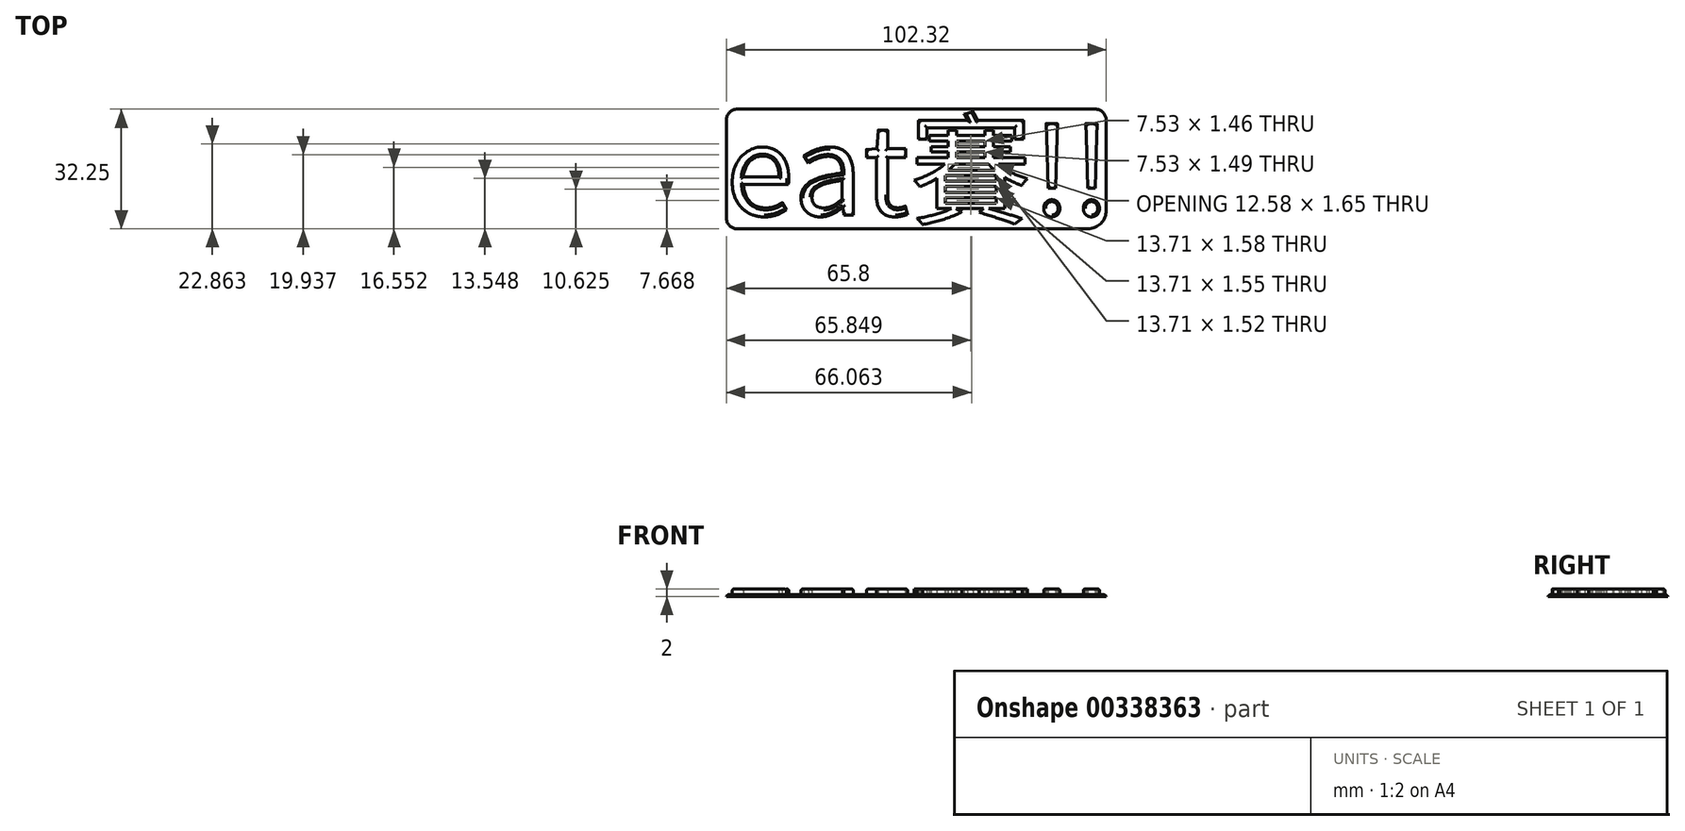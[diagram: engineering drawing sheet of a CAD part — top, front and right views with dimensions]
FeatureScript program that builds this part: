
annotation { "Feature Type Name" : "Feature", "Feature Type Description" : "" }
export const myFeature = defineFeature(function(context is Context, id is Id, definition is map)
    precondition{}
    {
        {
            var Q0;
            Q0=qCreatedBy(makeId("Top.planeOp"),FACE);
            var sketch = newSketch(context, id + "F0", { "sketchPlane" : qUnion([Q0])});
            skText(sketch, "E0", { "text": "eat賽!!", "fontName": "NotoSansCJKtc-Regular.otf"});
            const initialGuessF0  = {"E0": [-0.0526, 0.0191, 1, 0, 0.02378]};
            skSetInitialGuess(sketch, initialGuessF0);
            skSolve(sketch);
        }
        {
            var Q0;
            Q0 = qSketchRegion(id + "F0", true);
            extrude(context, id + "F1", {"entities" : qUnion([Q0]), "depth" : 1.5 * mm});
        }
        {
            var Q0;
            Q0=makeQuery(id+"F1.opExtrude","CAP_FACE",FACE,{"disambiguationData":[OSD([sQuery(id+"F0.wireOp",EDGE,"E0.sketch_text.stroke-0"),sQuery(id+"F0.wireOp",EDGE,"E0.sketch_text.stroke-1"),sQuery(id+"F0.wireOp",EDGE,"E0.sketch_text.stroke-2"),sQuery(id+"F0.wireOp",EDGE,"E0.sketch_text.stroke-3"),sQuery(id+"F0.wireOp",EDGE,"E0.sketch_text.stroke-4"),sQuery(id+"F0.wireOp",EDGE,"E0.sketch_text.stroke-5"),sQuery(id+"F0.wireOp",EDGE,"E0.sketch_text.stroke-6"),sQuery(id+"F0.wireOp",EDGE,"E0.sketch_text.stroke-7"),sQuery(id+"F0.wireOp",EDGE,"E0.sketch_text.stroke-8"),sQuery(id+"F0.wireOp",EDGE,"E0.sketch_text.stroke-9"),sQuery(id+"F0.wireOp",EDGE,"E0.sketch_text.stroke-10"),sQuery(id+"F0.wireOp",EDGE,"E0.sketch_text.stroke-11")])],"isStart":false});
            var Q1;
            Q1=makeQuery(id+"F1.opExtrude","CAP_FACE",FACE,{"disambiguationData":[OSD([sQuery(id+"F0.wireOp",EDGE,"E0.sketch_text.stroke-12"),sQuery(id+"F0.wireOp",EDGE,"E0.sketch_text.stroke-13"),sQuery(id+"F0.wireOp",EDGE,"E0.sketch_text.stroke-14"),sQuery(id+"F0.wireOp",EDGE,"E0.sketch_text.stroke-15"),sQuery(id+"F0.wireOp",EDGE,"E0.sketch_text.stroke-16"),sQuery(id+"F0.wireOp",EDGE,"E0.sketch_text.stroke-17"),sQuery(id+"F0.wireOp",EDGE,"E0.sketch_text.stroke-18"),sQuery(id+"F0.wireOp",EDGE,"E0.sketch_text.stroke-19"),sQuery(id+"F0.wireOp",EDGE,"E0.sketch_text.stroke-20"),sQuery(id+"F0.wireOp",EDGE,"E0.sketch_text.stroke-21"),sQuery(id+"F0.wireOp",EDGE,"E0.sketch_text.stroke-22"),sQuery(id+"F0.wireOp",EDGE,"E0.sketch_text.stroke-23"),sQuery(id+"F0.wireOp",EDGE,"E0.sketch_text.stroke-24"),sQuery(id+"F0.wireOp",EDGE,"E0.sketch_text.stroke-25"),sQuery(id+"F0.wireOp",EDGE,"E0.sketch_text.stroke-26"),sQuery(id+"F0.wireOp",EDGE,"E0.sketch_text.stroke-27")])],"isStart":false});
            var Q2;
            Q2=makeQuery(id+"F1.opExtrude","CAP_FACE",FACE,{"disambiguationData":[OSD([sQuery(id+"F0.wireOp",EDGE,"E0.sketch_text.stroke-28"),sQuery(id+"F0.wireOp",EDGE,"E0.sketch_text.stroke-29"),sQuery(id+"F0.wireOp",EDGE,"E0.sketch_text.stroke-30"),sQuery(id+"F0.wireOp",EDGE,"E0.sketch_text.stroke-31"),sQuery(id+"F0.wireOp",EDGE,"E0.sketch_text.stroke-32"),sQuery(id+"F0.wireOp",EDGE,"E0.sketch_text.stroke-33"),sQuery(id+"F0.wireOp",EDGE,"E0.sketch_text.stroke-34"),sQuery(id+"F0.wireOp",EDGE,"E0.sketch_text.stroke-35"),sQuery(id+"F0.wireOp",EDGE,"E0.sketch_text.stroke-36"),sQuery(id+"F0.wireOp",EDGE,"E0.sketch_text.stroke-37"),sQuery(id+"F0.wireOp",EDGE,"E0.sketch_text.stroke-38"),sQuery(id+"F0.wireOp",EDGE,"E0.sketch_text.stroke-39"),sQuery(id+"F0.wireOp",EDGE,"E0.sketch_text.stroke-40"),sQuery(id+"F0.wireOp",EDGE,"E0.sketch_text.stroke-41"),sQuery(id+"F0.wireOp",EDGE,"E0.sketch_text.stroke-42"),sQuery(id+"F0.wireOp",EDGE,"E0.sketch_text.stroke-43")])],"isStart":false});
            var Q3;
            Q3=makeQuery(id+"F1.opExtrude","CAP_FACE",FACE,{"disambiguationData":[OSD([sQuery(id+"F0.wireOp",EDGE,"E0.sketch_text.stroke-56"),sQuery(id+"F0.wireOp",EDGE,"E0.sketch_text.stroke-57"),sQuery(id+"F0.wireOp",EDGE,"E0.sketch_text.stroke-58"),sQuery(id+"F0.wireOp",EDGE,"E0.sketch_text.stroke-59"),sQuery(id+"F0.wireOp",EDGE,"E0.sketch_text.stroke-60"),sQuery(id+"F0.wireOp",EDGE,"E0.sketch_text.stroke-61"),sQuery(id+"F0.wireOp",EDGE,"E0.sketch_text.stroke-62"),sQuery(id+"F0.wireOp",EDGE,"E0.sketch_text.stroke-63"),sQuery(id+"F0.wireOp",EDGE,"E0.sketch_text.stroke-64"),sQuery(id+"F0.wireOp",EDGE,"E0.sketch_text.stroke-65"),sQuery(id+"F0.wireOp",EDGE,"E0.sketch_text.stroke-66"),sQuery(id+"F0.wireOp",EDGE,"E0.sketch_text.stroke-67"),sQuery(id+"F0.wireOp",EDGE,"E0.sketch_text.stroke-68"),sQuery(id+"F0.wireOp",EDGE,"E0.sketch_text.stroke-69"),sQuery(id+"F0.wireOp",EDGE,"E0.sketch_text.stroke-70"),sQuery(id+"F0.wireOp",EDGE,"E0.sketch_text.stroke-71"),sQuery(id+"F0.wireOp",EDGE,"E0.sketch_text.stroke-72"),sQuery(id+"F0.wireOp",EDGE,"E0.sketch_text.stroke-73"),sQuery(id+"F0.wireOp",EDGE,"E0.sketch_text.stroke-74"),sQuery(id+"F0.wireOp",EDGE,"E0.sketch_text.stroke-75"),sQuery(id+"F0.wireOp",EDGE,"E0.sketch_text.stroke-76"),sQuery(id+"F0.wireOp",EDGE,"E0.sketch_text.stroke-77"),sQuery(id+"F0.wireOp",EDGE,"E0.sketch_text.stroke-78"),sQuery(id+"F0.wireOp",EDGE,"E0.sketch_text.stroke-79"),sQuery(id+"F0.wireOp",EDGE,"E0.sketch_text.stroke-80"),sQuery(id+"F0.wireOp",EDGE,"E0.sketch_text.stroke-81"),sQuery(id+"F0.wireOp",EDGE,"E0.sketch_text.stroke-82"),sQuery(id+"F0.wireOp",EDGE,"E0.sketch_text.stroke-83"),sQuery(id+"F0.wireOp",EDGE,"E0.sketch_text.stroke-84"),sQuery(id+"F0.wireOp",EDGE,"E0.sketch_text.stroke-85"),sQuery(id+"F0.wireOp",EDGE,"E0.sketch_text.stroke-86"),sQuery(id+"F0.wireOp",EDGE,"E0.sketch_text.stroke-87"),sQuery(id+"F0.wireOp",EDGE,"E0.sketch_text.stroke-88"),sQuery(id+"F0.wireOp",EDGE,"E0.sketch_text.stroke-89"),sQuery(id+"F0.wireOp",EDGE,"E0.sketch_text.stroke-90"),sQuery(id+"F0.wireOp",EDGE,"E0.sketch_text.stroke-91"),sQuery(id+"F0.wireOp",EDGE,"E0.sketch_text.stroke-92"),sQuery(id+"F0.wireOp",EDGE,"E0.sketch_text.stroke-93"),sQuery(id+"F0.wireOp",EDGE,"E0.sketch_text.stroke-94"),sQuery(id+"F0.wireOp",EDGE,"E0.sketch_text.stroke-95"),sQuery(id+"F0.wireOp",EDGE,"E0.sketch_text.stroke-96"),sQuery(id+"F0.wireOp",EDGE,"E0.sketch_text.stroke-97"),sQuery(id+"F0.wireOp",EDGE,"E0.sketch_text.stroke-98"),sQuery(id+"F0.wireOp",EDGE,"E0.sketch_text.stroke-99"),sQuery(id+"F0.wireOp",EDGE,"E0.sketch_text.stroke-100"),sQuery(id+"F0.wireOp",EDGE,"E0.sketch_text.stroke-101"),sQuery(id+"F0.wireOp",EDGE,"E0.sketch_text.stroke-102"),sQuery(id+"F0.wireOp",EDGE,"E0.sketch_text.stroke-103"),sQuery(id+"F0.wireOp",EDGE,"E0.sketch_text.stroke-104"),sQuery(id+"F0.wireOp",EDGE,"E0.sketch_text.stroke-105"),sQuery(id+"F0.wireOp",EDGE,"E0.sketch_text.stroke-106"),sQuery(id+"F0.wireOp",EDGE,"E0.sketch_text.stroke-107"),sQuery(id+"F0.wireOp",EDGE,"E0.sketch_text.stroke-108"),sQuery(id+"F0.wireOp",EDGE,"E0.sketch_text.stroke-109"),sQuery(id+"F0.wireOp",EDGE,"E0.sketch_text.stroke-110"),sQuery(id+"F0.wireOp",EDGE,"E0.sketch_text.stroke-111"),sQuery(id+"F0.wireOp",EDGE,"E0.sketch_text.stroke-112"),sQuery(id+"F0.wireOp",EDGE,"E0.sketch_text.stroke-113"),sQuery(id+"F0.wireOp",EDGE,"E0.sketch_text.stroke-114"),sQuery(id+"F0.wireOp",EDGE,"E0.sketch_text.stroke-115"),sQuery(id+"F0.wireOp",EDGE,"E0.sketch_text.stroke-116"),sQuery(id+"F0.wireOp",EDGE,"E0.sketch_text.stroke-117"),sQuery(id+"F0.wireOp",EDGE,"E0.sketch_text.stroke-118"),sQuery(id+"F0.wireOp",EDGE,"E0.sketch_text.stroke-119"),sQuery(id+"F0.wireOp",EDGE,"E0.sketch_text.stroke-120"),sQuery(id+"F0.wireOp",EDGE,"E0.sketch_text.stroke-121"),sQuery(id+"F0.wireOp",EDGE,"E0.sketch_text.stroke-122"),sQuery(id+"F0.wireOp",EDGE,"E0.sketch_text.stroke-123"),sQuery(id+"F0.wireOp",EDGE,"E0.sketch_text.stroke-124"),sQuery(id+"F0.wireOp",EDGE,"E0.sketch_text.stroke-125"),sQuery(id+"F0.wireOp",EDGE,"E0.sketch_text.stroke-126"),sQuery(id+"F0.wireOp",EDGE,"E0.sketch_text.stroke-127")])],"isStart":false});
            var Q4;
            Q4=makeQuery(id+"F1.opExtrude","CAP_FACE",FACE,{"disambiguationData":[OSD([sQuery(id+"F0.wireOp",EDGE,"E0.sketch_text.stroke-44"),sQuery(id+"F0.wireOp",EDGE,"E0.sketch_text.stroke-45"),sQuery(id+"F0.wireOp",EDGE,"E0.sketch_text.stroke-46"),sQuery(id+"F0.wireOp",EDGE,"E0.sketch_text.stroke-47"),sQuery(id+"F0.wireOp",EDGE,"E0.sketch_text.stroke-48"),sQuery(id+"F0.wireOp",EDGE,"E0.sketch_text.stroke-49"),sQuery(id+"F0.wireOp",EDGE,"E0.sketch_text.stroke-50"),sQuery(id+"F0.wireOp",EDGE,"E0.sketch_text.stroke-51"),sQuery(id+"F0.wireOp",EDGE,"E0.sketch_text.stroke-52"),sQuery(id+"F0.wireOp",EDGE,"E0.sketch_text.stroke-53"),sQuery(id+"F0.wireOp",EDGE,"E0.sketch_text.stroke-54"),sQuery(id+"F0.wireOp",EDGE,"E0.sketch_text.stroke-55")])],"isStart":false});
            var Q5;
            Q5=makeQuery(id+"F1.opExtrude","CAP_FACE",FACE,{"disambiguationData":[OSD([sQuery(id+"F0.wireOp",EDGE,"E0.sketch_text.stroke-128"),sQuery(id+"F0.wireOp",EDGE,"E0.sketch_text.stroke-129"),sQuery(id+"F0.wireOp",EDGE,"E0.sketch_text.stroke-130"),sQuery(id+"F0.wireOp",EDGE,"E0.sketch_text.stroke-131"),sQuery(id+"F0.wireOp",EDGE,"E0.sketch_text.stroke-132"),sQuery(id+"F0.wireOp",EDGE,"E0.sketch_text.stroke-133")])],"isStart":false});
            var Q6;
            Q6=makeQuery(id+"F1.opExtrude","CAP_FACE",FACE,{"disambiguationData":[OSD([sQuery(id+"F0.wireOp",EDGE,"E0.sketch_text.stroke-134"),sQuery(id+"F0.wireOp",EDGE,"E0.sketch_text.stroke-135"),sQuery(id+"F0.wireOp",EDGE,"E0.sketch_text.stroke-136"),sQuery(id+"F0.wireOp",EDGE,"E0.sketch_text.stroke-137")])],"isStart":false});
            var Q7;
            Q7=makeQuery(id+"F1.opExtrude","CAP_FACE",FACE,{"disambiguationData":[OSD([sQuery(id+"F0.wireOp",EDGE,"E0.sketch_text.stroke-144"),sQuery(id+"F0.wireOp",EDGE,"E0.sketch_text.stroke-145"),sQuery(id+"F0.wireOp",EDGE,"E0.sketch_text.stroke-146"),sQuery(id+"F0.wireOp",EDGE,"E0.sketch_text.stroke-147")])],"isStart":false});
            var Q8;
            Q8=makeQuery(id+"F1.opExtrude","CAP_FACE",FACE,{"disambiguationData":[OSD([sQuery(id+"F0.wireOp",EDGE,"E0.sketch_text.stroke-138"),sQuery(id+"F0.wireOp",EDGE,"E0.sketch_text.stroke-139"),sQuery(id+"F0.wireOp",EDGE,"E0.sketch_text.stroke-140"),sQuery(id+"F0.wireOp",EDGE,"E0.sketch_text.stroke-141"),sQuery(id+"F0.wireOp",EDGE,"E0.sketch_text.stroke-142"),sQuery(id+"F0.wireOp",EDGE,"E0.sketch_text.stroke-143")])],"isStart":false});
            fillet(context, id + "F2", {"entities" : qUnion([Q0, Q1, Q2, Q3, Q4, Q5, Q6, Q7, Q8]), "radius" : .5 * mm, "tangentPropagation" : true, "allowEdgeOverflow" : false});
        }
        {
            var Q0;
            Q0=qCreatedBy(makeId("Top.planeOp"),FACE);
            var sketch = newSketch(context, id + "F3", { "sketchPlane" : qUnion([Q0])});
            skLineSegment(sketch, "E1.bottom", {"start": v(46.8, 47.71) * mm, "end": v(-49.52, 47.71) * mm});
            skLineSegment(sketch, "E1.top", {"start": v(44.8, 15.46) * mm, "end": v(-49.52, 15.46) * mm});
            skLineSegment(sketch, "E1.left", {"start": v(49.8, 44.71) * mm, "end": v(49.8, 20.46) * mm});
            skLineSegment(sketch, "E1.right", {"start": v(-52.52, 44.71) * mm, "end": v(-52.52, 18.46) * mm});
            skPoint(sketch, "E2.visualSharp", {"position": v(49.8, 15.46) * mm});
            skArc(sketch, "E2.filletArc", {"start": v(44.8, 15.46) * mm, "mid": v(48.34, 16.93) * mm, "end": v(49.8, 20.46) * mm});
            skPoint(sketch, "E3.visualSharp", {"position": v(49.8, 47.71) * mm});
            skArc(sketch, "E3.filletArc", {"start": v(49.8, 44.71) * mm, "mid": v(48.92, 46.83) * mm, "end": v(46.8, 47.71) * mm});
            skPoint(sketch, "E4.visualSharp", {"position": v(-52.52, 47.71) * mm});
            skArc(sketch, "E4.filletArc", {"start": v(-49.52, 47.71) * mm, "mid": v(-51.65, 46.83) * mm, "end": v(-52.52, 44.71) * mm});
            skPoint(sketch, "E5.visualSharp", {"position": v(-52.52, 15.46) * mm});
            skArc(sketch, "E5.filletArc", {"start": v(-52.52, 18.46) * mm, "mid": v(-51.65, 16.34) * mm, "end": v(-49.52, 15.46) * mm});
            skSolve(sketch);
        }
        {
            var Q0;
            Q0 = qSketchRegion(id + "F3", true);
            extrude(context, id + "F4", {"entities" : qUnion([Q0]), "oppositeDirection" : true, "depth" : .5 * mm});
        }
        {
            var Q0;
            Q0=makeQuery(id+"F4.opExtrude","CAP_FACE",FACE,{"disambiguationData":[OSD([sQuery(id+"F3.wireOp",EDGE,"E1.bottom"),sQuery(id+"F3.wireOp",EDGE,"E1.top"),sQuery(id+"F3.wireOp",EDGE,"E1.left"),sQuery(id+"F3.wireOp",EDGE,"E1.right"),sQuery(id+"F3.wireOp",EDGE,"E2.filletArc"),sQuery(id+"F3.wireOp",EDGE,"E3.filletArc"),sQuery(id+"F3.wireOp",EDGE,"E4.filletArc"),sQuery(id+"F3.wireOp",EDGE,"E5.filletArc")])],"isStart":true});
            fillet(context, id + "F5", {"entities" : qUnion([Q0]), "radius" : 1.2 * mm, "tangentPropagation" : true, "allowEdgeOverflow" : false});
        }
    });
